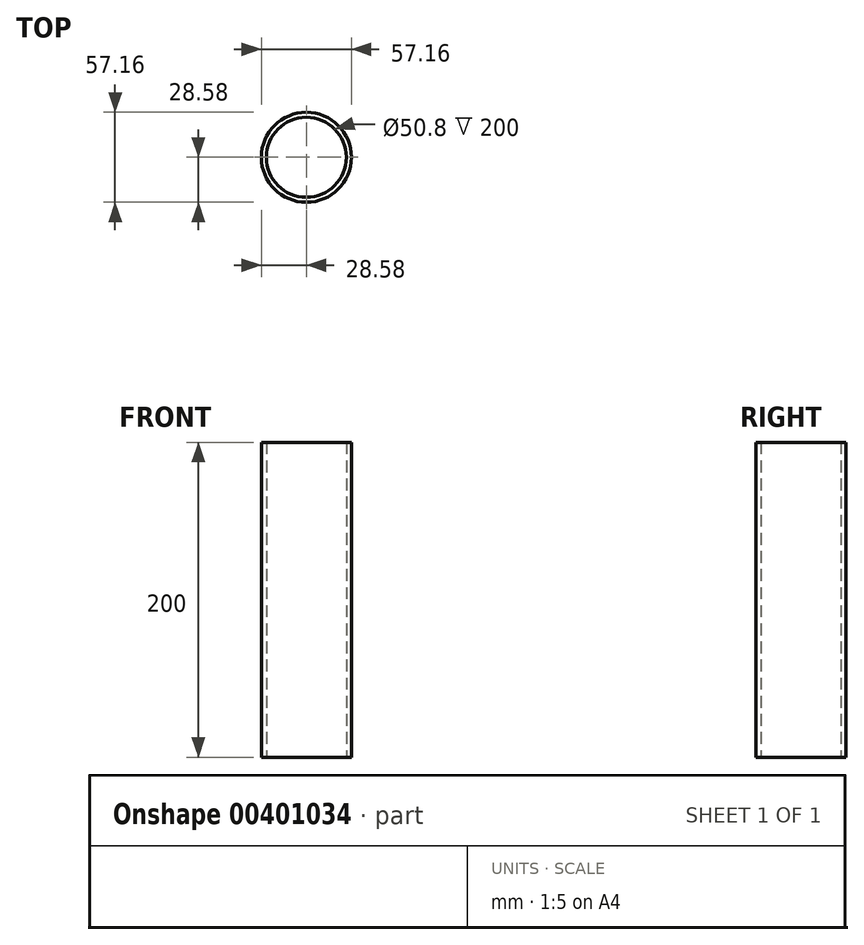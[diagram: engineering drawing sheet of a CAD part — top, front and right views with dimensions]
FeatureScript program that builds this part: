
annotation { "Feature Type Name" : "Feature", "Feature Type Description" : "" }
export const myFeature = defineFeature(function(context is Context, id is Id, definition is map)
    precondition{}
    {
        {
            var Q0;
            Q0=qCreatedBy(makeId("Top.planeOp"),FACE);
            var sketch = newSketch(context, id + "F0", { "sketchPlane" : qUnion([Q0])});
            skCircle(sketch, "E0", {"center": v(0, 0) * mm, "radius": 25.4 * mm});
            skCircle(sketch, "E1.0", {"center": v(0, 0) * mm, "radius": 28.58 * mm});
            skSolve(sketch);
        }
        {
            var Q0;
            Q0=makeQuery(id+"F0.imprint","IMPRINT",FACE,{"disambiguationData":[TD([[makeQuery(id+"F0.imprint","IMPRINT",EDGE,{"derivedFrom":sQuery(id+"F0.wireOp",EDGE,"E0")}),-1.0]])]});
            extrude(context, id + "F1", {"entities" : qUnion([Q0]), "depth" : 200 * mm});
        }
    });
